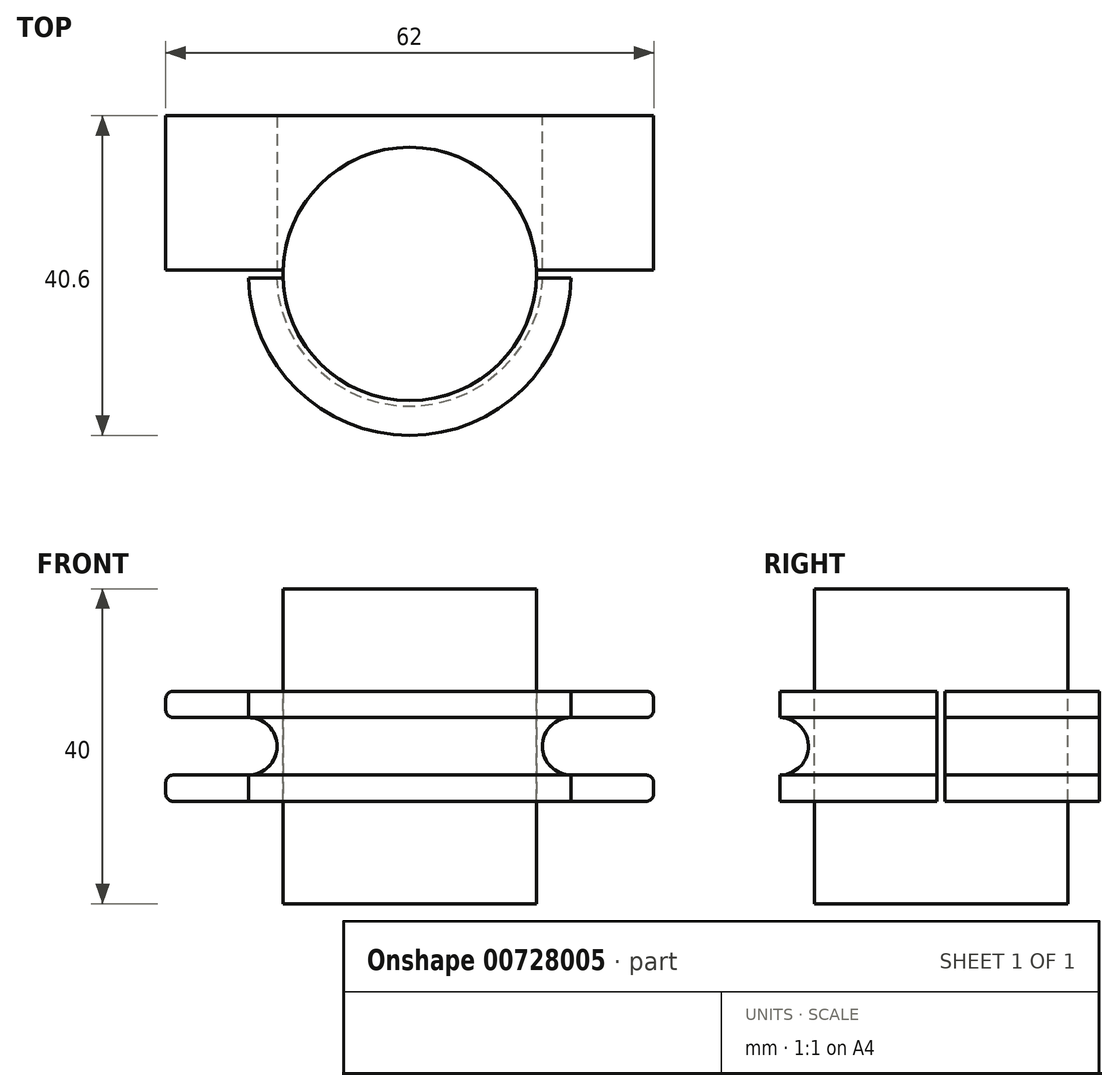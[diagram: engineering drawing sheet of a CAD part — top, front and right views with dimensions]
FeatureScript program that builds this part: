
annotation { "Feature Type Name" : "Feature", "Feature Type Description" : "" }
export const myFeature = defineFeature(function(context is Context, id is Id, definition is map)
    precondition{}
    {
        {
            var Q0;
            Q0=qCreatedBy(makeId("Top.planeOp"),FACE);
            var sketch = newSketch(context, id + "F0", { "sketchPlane" : qUnion([Q0])});
            skArc(sketch, "E0", {"start": v(-20.5, 0) * mm, "mid": v(0, -20.5) * mm, "end": v(20.5, 0) * mm});
            skLineSegment(sketch, "E1", {"start": v(20.5, 0) * mm, "end": v(20.5, 60) * mm});
            skLineSegment(sketch, "E2", {"start": v(-20.5, 0) * mm, "end": v(-20.5, 60) * mm});
            skCircle(sketch, "E3", {"center": v(0, 0) * mm, "radius": 16.1 * mm});
            skLineSegment(sketch, "E4", {"start": v(-20.5, -0.5) * mm, "end": v(20.5, -0.5) * mm});
            skLineSegment(sketch, "E5", {"start": v(-20.5, 0.5) * mm, "end": v(20.5, 0.5) * mm});
            skLineSegment(sketch, "E6", {"start": v(-20.5, 20.1) * mm, "end": v(20.5, 20.1) * mm});
            skArc(sketch, "E7", {"start": v(31, -0.5) * mm, "mid": v(0, -31) * mm, "end": v(-31, -0.5) * mm});
            skLineSegment(sketch, "E8", {"start": v(31, -0.5) * mm, "end": v(31, 20.1) * mm});
            skLineSegment(sketch, "E9", {"start": v(31, 20.1) * mm, "end": v(20.5, 20.1) * mm});
            skLineSegment(sketch, "E10", {"start": v(-31, -0.5) * mm, "end": v(-31, 20.1) * mm});
            skLineSegment(sketch, "E11", {"start": v(-31, 20.1) * mm, "end": v(-20.5, 20.1) * mm});
            skLineSegment(sketch, "E12", {"start": v(-20.5, -0.5) * mm, "end": v(-31, -0.5) * mm});
            skLineSegment(sketch, "E13", {"start": v(20.5, -0.5) * mm, "end": v(31, -0.5) * mm});
            skLineSegment(sketch, "E14", {"start": v(20.5, 0.5) * mm, "end": v(31, 0.5) * mm});
            skLineSegment(sketch, "E15", {"start": v(31, 0.5) * mm, "end": v(-20.5, 0.5) * mm});
            skLineSegment(sketch, "E16", {"start": v(-20.5, 0.5) * mm, "end": v(-31, 0.5) * mm});
            skSolve(sketch);
        }
        {
            var Q0;
            Q0=qCreatedBy(makeId("Front.planeOp"),FACE);
            var sketch = newSketch(context, id + "F1", { "sketchPlane" : qUnion([Q0])});
            skCircle(sketch, "E17", {"center": v(20.5, 0) * mm, "radius": 3.65 * mm});
            skLineSegment(sketch, "E18", {"start": v(0, 0) * mm, "end": v(0, -20) * mm});
            skLineSegment(sketch, "E19", {"start": v(0, 0) * mm, "end": v(0, 20) * mm});
            skLineSegment(sketch, "E20", {"start": v(20.5, 3.65) * mm, "end": v(31.2, 3.65) * mm});
            skLineSegment(sketch, "E21", {"start": v(31.2, 3.65) * mm, "end": v(31.2, -3.65) * mm});
            skLineSegment(sketch, "E22", {"start": v(31.2, -3.65) * mm, "end": v(20.5, -3.65) * mm});
            skSolve(sketch);
        }
        {
            var Q0;
            Q0=makeQuery(id+"F1.imprint","IMPRINT",FACE,{"disambiguationData":[TD([[makeQuery(id+"F1.imprint","IMPRINT",EDGE,{"derivedFrom":sQuery(id+"F1.wireOp",EDGE,"E17")}),1.0]])]});
            var Q1;
            Q1=sQuery(id+"F0.wireOp",EDGE,"E0");
            var Q2;
            Q2=sQuery(id+"F0.wireOp",EDGE,"E1");
            var Q3;
            Q3=sQuery(id+"F0.wireOp",EDGE,"E2");
            sweep(context, id + "F2", {"profiles" : qUnion([Q0]), "path" : qUnion([Q1, Q2, Q3])});
        }
        {
            var Q0;
            Q0=makeQuery(id+"F0.imprint","IMPRINT",FACE,{"disambiguationData":[TD([[makeQuery(id+"F0.imprint","IMPRINT",EDGE,{"derivedFrom":sQuery(id+"F0.wireOp",EDGE,"E3")}),1.0]])]});
            var Q1;
            {var subQ0=sQuery(id+"F0.wireOp",EDGE,"E5");var subQ1=sQuery(id+"F0.wireOp",EDGE,"E3");var subQ2=makeQuery(id+"F0.imprint","INTERSECT",VERTEX,{"disambiguationData":[OD(0.0)],"derivedFrom":[subQ1,subQ0]});Q1=makeQuery(id+"F0.imprint","IMPRINT",FACE,{"disambiguationData":[TD([[makeQuery(id+"F0.imprint","IMPRINT",EDGE,{"disambiguationData":[TD([[subQ2,1.0]])],"derivedFrom":subQ1}),1.0]])]});}
            var Q2;
            {var subQ0=sQuery(id+"F0.wireOp",EDGE,"E4");var subQ1=sQuery(id+"F0.wireOp",EDGE,"E3");var subQ2=makeQuery(id+"F0.imprint","INTERSECT",VERTEX,{"disambiguationData":[OD(0.0)],"derivedFrom":[subQ1,subQ0]});Q2=makeQuery(id+"F0.imprint","IMPRINT",FACE,{"disambiguationData":[TD([[makeQuery(id+"F0.imprint","IMPRINT",EDGE,{"disambiguationData":[TD([[subQ2,-1.0]])],"derivedFrom":subQ1}),1.0]])]});}
            var Q3;
            {var subQ0=sQuery(id+"F0.wireOp",EDGE,"E15");var subQ1=sQuery(id+"F0.wireOp",EDGE,"E3");var subQ2=makeQuery(id+"F0.imprint","INTERSECT",VERTEX,{"disambiguationData":[OD(0.0)],"derivedFrom":[subQ1,subQ0]});Q3=makeQuery(id+"F0.imprint","IMPRINT",FACE,{"disambiguationData":[TD([[makeQuery(id+"F0.imprint","IMPRINT",EDGE,{"disambiguationData":[TD([[subQ2,1.0]])],"derivedFrom":subQ1}),1.0]])]});}
            var Q4;
            Q4=sQuery(id+"F1.wireOp",EDGE,"E18");
            var Q5;
            Q5=sQuery(id+"F1.wireOp",EDGE,"E19");
            sweep(context, id + "F3", {"profiles" : qUnion([Q0, Q1, Q2, Q3]), "path" : qUnion([Q4, Q5])});
        }
        {
            var Q0;
            {var subQ6=sQuery(id+"F0.wireOp",EDGE,"E6");Q0=makeQuery(id+"F0.imprint","IMPRINT",FACE,{"disambiguationData":[TD([[makeQuery(id+"F0.imprint","IMPRINT",EDGE,{"derivedFrom":subQ6}),-1.0]])]});}
            var Q1;
            {var subQ0=sQuery(id+"F0.wireOp",EDGE,"E4");var subQ1=sQuery(id+"F0.wireOp",EDGE,"E0");var subQ2=makeQuery(id+"F0.imprint","INTERSECT",VERTEX,{"disambiguationData":[OD(0.0)],"derivedFrom":[subQ1,subQ0]});Q1=makeQuery(id+"F0.imprint","IMPRINT",FACE,{"disambiguationData":[TD([[makeQuery(id+"F0.imprint","IMPRINT",EDGE,{"disambiguationData":[TD([[subQ2,-1.0]])],"derivedFrom":subQ1}),1.0]])]});}
            var Q2;
            {var subQ0=sQuery(id+"F0.wireOp",EDGE,"E11");Q2=makeQuery(id+"F0.imprint","IMPRINT",FACE,{"disambiguationData":[TD([[makeQuery(id+"F0.imprint","IMPRINT",EDGE,{"derivedFrom":subQ0}),-1.0]])]});}
            var Q3;
            {var subQ0=sQuery(id+"F0.wireOp",EDGE,"E9");Q3=makeQuery(id+"F0.imprint","IMPRINT",FACE,{"disambiguationData":[TD([[makeQuery(id+"F0.imprint","IMPRINT",EDGE,{"derivedFrom":subQ0}),1.0]])]});}
            var Q4;
            Q4=makeQuery(id+"F0.imprint","IMPRINT",FACE,{"disambiguationData":[TD([[makeQuery(id+"F0.imprint","IMPRINT",EDGE,{"derivedFrom":sQuery(id+"F0.wireOp",EDGE,"E7")}),-1.0]])]});
            extrude(context, id + "F4", {"entities" : qUnion([Q0, Q1, Q2, Q3, Q4]), "depth" : 7 * mm, "offsetDistance" : 25 * mm, "hasSecondDirection" : true, "secondDirectionOppositeDirection" : true, "secondDirectionDepth" : 7 * mm});
        }
        {
            var Q0;
            {var subQ0=sQuery(id+"F1.wireOp",EDGE,"E17");var subQ1=makeQuery(id+"F1.imprint","INTERSECT",VERTEX,{"derivedFrom":[subQ0,sQuery(id+"F1.wireOp",EDGE,"E20")]});Q0=makeQuery(id+"F1.imprint","IMPRINT",FACE,{"disambiguationData":[TD([[makeQuery(id+"F1.imprint","IMPRINT",EDGE,{"disambiguationData":[TD([[subQ1,-1.0]])],"derivedFrom":subQ0}),1.0]])]});}
            var Q1;
            {var subQ0=sQuery(id+"F1.wireOp",EDGE,"E20");Q1=makeQuery(id+"F1.imprint","IMPRINT",FACE,{"disambiguationData":[TD([[makeQuery(id+"F1.imprint","IMPRINT",EDGE,{"derivedFrom":subQ0}),-1.0]])]});}
            var Q2;
            Q2=sQuery(id+"F0.wireOp",EDGE,"E1");
            var Q3;
            Q3=sQuery(id+"F0.wireOp",EDGE,"E0");
            var Q4;
            Q4=sQuery(id+"F0.wireOp",EDGE,"E2");
            sweep(context, id + "F5", {"operationType" : NewBodyOperationType.REMOVE, "profiles" : qUnion([Q0, Q1]), "path" : qUnion([Q2, Q3, Q4])});
        }
        {
            var Q0;
            Q0=makeQuery(id+"F4.opExtrude","CAP_EDGE",EDGE,{"disambiguationData":[OSD([sQuery(id+"F0.wireOp",EDGE,"E8")])],"isStart":false});
            var Q1;
            Q1=makeQuery(id+"F5.boolean.opBoolean","INTERSECT",EDGE,{"derivedFrom":[makeQuery(id+"F4.opExtrude","SWEPT_FACE",FACE,{"disambiguationData":[OSD([sQuery(id+"F0.wireOp",EDGE,"E8")])]}),makeQuery(id+"F5.opSweep","SWEPT_FACE",FACE,{"disambiguationData":[OSD([sQuery(id+"F0.wireOp",EDGE,"E1"),sQuery(id+"F1.wireOp",EDGE,"E20")])]})]});
            var Q2;
            Q2=makeQuery(id+"F5.boolean.opBoolean","INTERSECT",EDGE,{"derivedFrom":[makeQuery(id+"F4.opExtrude","SWEPT_FACE",FACE,{"disambiguationData":[OSD([sQuery(id+"F0.wireOp",EDGE,"E8")])]}),makeQuery(id+"F5.opSweep","SWEPT_FACE",FACE,{"disambiguationData":[OSD([sQuery(id+"F0.wireOp",EDGE,"E1"),sQuery(id+"F1.wireOp",EDGE,"E22")])]})]});
            var Q3;
            Q3=makeQuery(id+"F4.opExtrude","CAP_EDGE",EDGE,{"disambiguationData":[OSD([sQuery(id+"F0.wireOp",EDGE,"E8")])],"isStart":true});
            var Q4;
            Q4=makeQuery(id+"F5.boolean.opBoolean","INTERSECT",EDGE,{"derivedFrom":[makeQuery(id+"F4.opExtrude","SWEPT_FACE",FACE,{"disambiguationData":[OSD([sQuery(id+"F0.wireOp",EDGE,"E7")])]}),makeQuery(id+"F5.opSweep","SWEPT_FACE",FACE,{"disambiguationData":[OSD([sQuery(id+"F0.wireOp",EDGE,"E1"),sQuery(id+"F1.wireOp",EDGE,"E22")])]})]});
            var Q5;
            Q5=makeQuery(id+"F4.opExtrude","CAP_EDGE",EDGE,{"disambiguationData":[OSD([sQuery(id+"F0.wireOp",EDGE,"E7")])],"isStart":true});
            var Q6;
            Q6=makeQuery(id+"F4.opExtrude","CAP_EDGE",EDGE,{"disambiguationData":[OSD([sQuery(id+"F0.wireOp",EDGE,"E7")])],"isStart":false});
            var Q7;
            Q7=makeQuery(id+"F5.boolean.opBoolean","INTERSECT",EDGE,{"derivedFrom":[makeQuery(id+"F4.opExtrude","SWEPT_FACE",FACE,{"disambiguationData":[OSD([sQuery(id+"F0.wireOp",EDGE,"E7")])]}),makeQuery(id+"F5.opSweep","SWEPT_FACE",FACE,{"disambiguationData":[OSD([sQuery(id+"F0.wireOp",EDGE,"E1"),sQuery(id+"F1.wireOp",EDGE,"E20")])]})]});
            var Q8;
            Q8=makeQuery(id+"F4.opExtrude","CAP_EDGE",EDGE,{"disambiguationData":[OSD([sQuery(id+"F0.wireOp",EDGE,"E10")])],"isStart":false});
            var Q9;
            Q9=makeQuery(id+"F5.boolean.opBoolean","INTERSECT",EDGE,{"derivedFrom":[makeQuery(id+"F4.opExtrude","SWEPT_FACE",FACE,{"disambiguationData":[OSD([sQuery(id+"F0.wireOp",EDGE,"E10")])]}),makeQuery(id+"F5.opSweep","SWEPT_FACE",FACE,{"disambiguationData":[OSD([sQuery(id+"F0.wireOp",EDGE,"E1"),sQuery(id+"F1.wireOp",EDGE,"E20")])]})]});
            var Q10;
            Q10=makeQuery(id+"F5.boolean.opBoolean","INTERSECT",EDGE,{"derivedFrom":[makeQuery(id+"F4.opExtrude","SWEPT_FACE",FACE,{"disambiguationData":[OSD([sQuery(id+"F0.wireOp",EDGE,"E10")])]}),makeQuery(id+"F5.opSweep","SWEPT_FACE",FACE,{"disambiguationData":[OSD([sQuery(id+"F0.wireOp",EDGE,"E1"),sQuery(id+"F1.wireOp",EDGE,"E22")])]})]});
            var Q11;
            Q11=makeQuery(id+"F4.opExtrude","CAP_EDGE",EDGE,{"disambiguationData":[OSD([sQuery(id+"F0.wireOp",EDGE,"E10")])],"isStart":true});
            fillet(context, id + "F6", {"entities" : qUnion([Q0, Q1, Q2, Q3, Q4, Q5, Q6, Q7, Q8, Q9, Q10, Q11]), "radius" : 1 * mm, "tangentPropagation" : true, "allowEdgeOverflow" : false});
        }
    });
